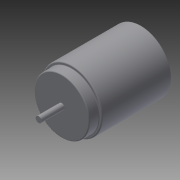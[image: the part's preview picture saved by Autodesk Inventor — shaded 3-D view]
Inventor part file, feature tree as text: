
AUTODESK INVENTOR PART (.ipt)
format: ipt  version: 2015 (Build 190159000, 159)  size: 119,296 bytes
history: native  units: in
note: dims shown in document units (in); Inventor stores cm internally (conversion verified against a paired STEP export)
features: extrude x3, sketch x2, fillet x2
ambient origin geometry x8: Origin, YZ Plane, XZ Plane, XY Plane, X Axis, Y Axis, Z Axis, Center Point
bodies: Solid1 (feature_tree)
feature tree (7):
  sketch  "Sketch1"  dims[d0=0.08in d1=0.82in]
  extrude  "Extrusion1"  Depth=0.82in
  extrude  "Extrusion2"  Depth=1.075in TaperAngle=0.0deg
  extrude  "Extrusion3"  Depth=0.007in
  fillet  "Fillet1"  Radius=0.135in
  fillet  "Fillet2"  Radius=0.014in
  sketch  "Sketch2"  dims[d2=0.31in d3=0.0in d4=1.075in d5=0.0in d6=0.745in d7=0.135in d8=0.0in d9=0.014in d10=0.007in]
